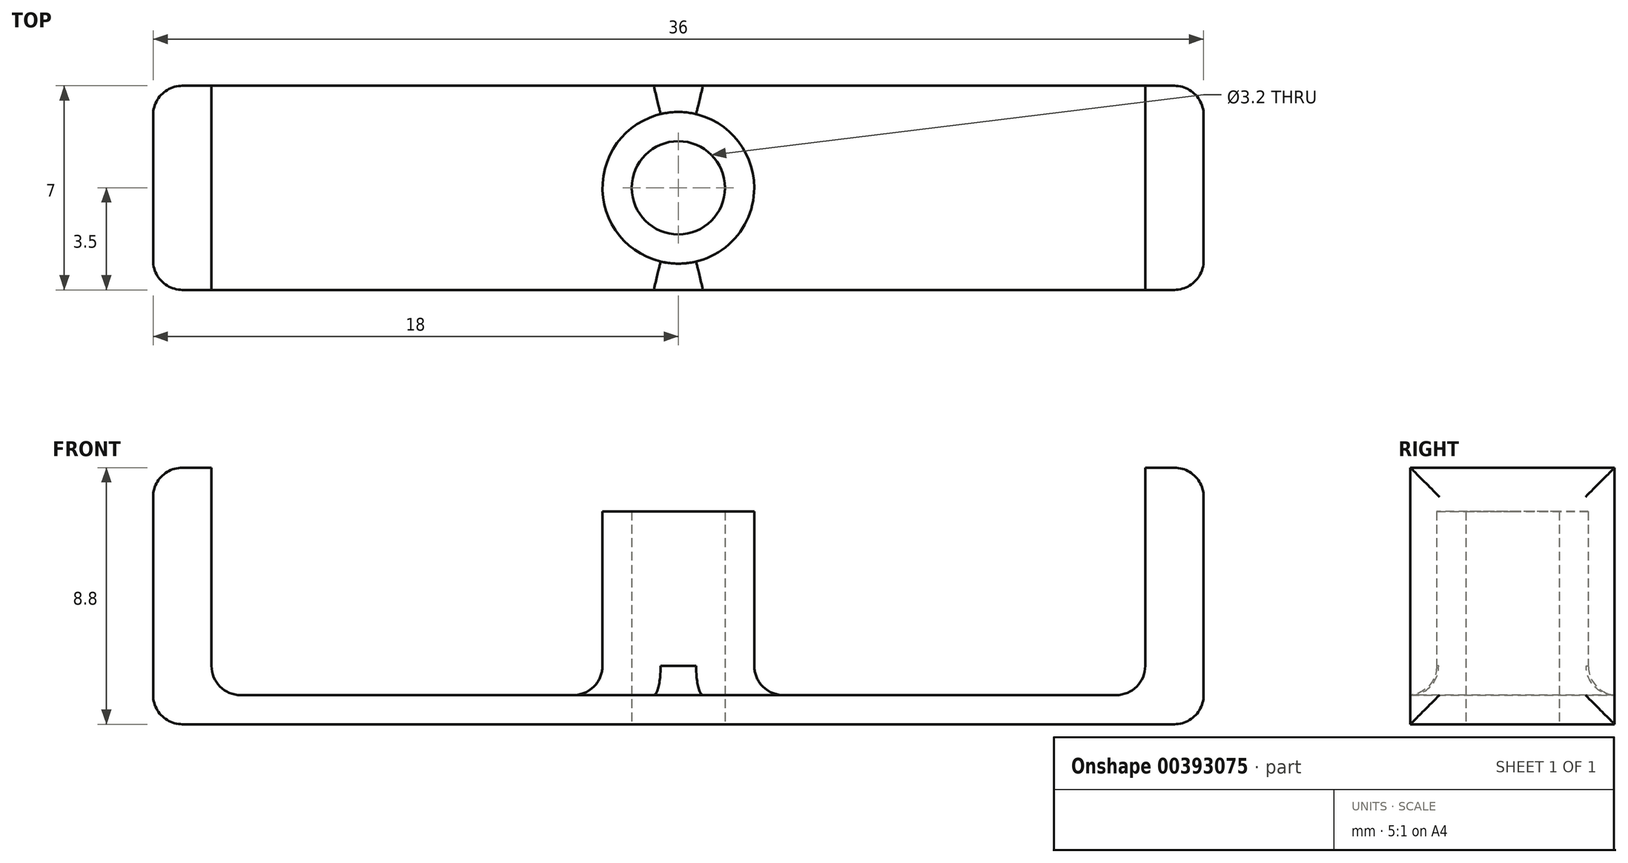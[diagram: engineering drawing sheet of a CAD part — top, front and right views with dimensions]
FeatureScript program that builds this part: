
annotation { "Feature Type Name" : "Feature", "Feature Type Description" : "" }
export const myFeature = defineFeature(function(context is Context, id is Id, definition is map)
    precondition{}
    {
        {
            var Q0;
            Q0=qCreatedBy(makeId("Top.planeOp"),FACE);
            var sketch = newSketch(context, id + "F0", { "sketchPlane" : qUnion([Q0])});
            skLineSegment(sketch, "E0.bottom", {"start": v(18, -3.5) * mm, "end": v(-18, -3.5) * mm});
            skLineSegment(sketch, "E0.top", {"start": v(18, 3.5) * mm, "end": v(-18, 3.5) * mm});
            skLineSegment(sketch, "E0.left", {"start": v(18, -3.5) * mm, "end": v(18, 3.5) * mm});
            skLineSegment(sketch, "E0.right", {"start": v(-18, -3.5) * mm, "end": v(-18, 3.5) * mm});
            skPoint(sketch, "E0.middle", {"position": v(0, 0) * mm});
            skCircle(sketch, "E1", {"center": v(0, 0) * mm, "radius": 1.6 * mm});
            skCircle(sketch, "E2.0", {"center": v(0, 0) * mm, "radius": 2.6 * mm});
            skLineSegment(sketch, "E3", {"start": v(-16, 3.5) * mm, "end": v(-16, -3.5) * mm});
            skLineSegment(sketch, "E4.MirrorCS", {"start": v(16, 3.5) * mm, "end": v(16, -3.5) * mm});
            skSolve(sketch);
        }
        {
            var Q0;
            Q0=makeQuery(id+"F0.imprint","IMPRINT",FACE,{"disambiguationData":[TD([[makeQuery(id+"F0.imprint","IMPRINT",EDGE,{"derivedFrom":sQuery(id+"F0.wireOp",EDGE,"E2.0")}),-1.0]])]});
            var Q1;
            {var subQ0=sQuery(id+"F0.wireOp",EDGE,"E0.right");Q1=makeQuery(id+"F0.imprint","IMPRINT",FACE,{"disambiguationData":[TD([[makeQuery(id+"F0.imprint","IMPRINT",EDGE,{"derivedFrom":subQ0}),-1.0]])]});}
            var Q2;
            {var subQ0=sQuery(id+"F0.wireOp",EDGE,"E0.left");Q2=makeQuery(id+"F0.imprint","IMPRINT",FACE,{"disambiguationData":[TD([[makeQuery(id+"F0.imprint","IMPRINT",EDGE,{"derivedFrom":subQ0}),1.0]])]});}
            var Q3;
            Q3=makeQuery(id+"F0.imprint","IMPRINT",FACE,{"disambiguationData":[TD([[makeQuery(id+"F0.imprint","IMPRINT",EDGE,{"derivedFrom":sQuery(id+"F0.wireOp",EDGE,"E1")}),-1.0]])]});
            extrude(context, id + "F1", {"entities" : qUnion([Q0, Q1, Q2, Q3]), "depth" : 1 * mm});
        }
        {
            var Q0;
            {var subQ0=sQuery(id+"F0.wireOp",EDGE,"E0.right");Q0=makeQuery(id+"F0.imprint","IMPRINT",FACE,{"disambiguationData":[TD([[makeQuery(id+"F0.imprint","IMPRINT",EDGE,{"derivedFrom":subQ0}),-1.0]])]});}
            var Q1;
            {var subQ0=sQuery(id+"F0.wireOp",EDGE,"E0.left");Q1=makeQuery(id+"F0.imprint","IMPRINT",FACE,{"disambiguationData":[TD([[makeQuery(id+"F0.imprint","IMPRINT",EDGE,{"derivedFrom":subQ0}),1.0]])]});}
            extrude(context, id + "F2", {"entities" : qUnion([Q0, Q1]), "operationType" : NewBodyOperationType.ADD, "depth" : 8.8 * mm});
        }
        {
            var Q0;
            Q0=makeQuery(id+"F0.imprint","IMPRINT",FACE,{"disambiguationData":[TD([[makeQuery(id+"F0.imprint","IMPRINT",EDGE,{"derivedFrom":sQuery(id+"F0.wireOp",EDGE,"E1")}),-1.0]])]});
            extrude(context, id + "F3", {"entities" : qUnion([Q0]), "operationType" : NewBodyOperationType.ADD, "depth" : 7.3 * mm});
        }
        {
            var Q0;
            Q0=makeQuery(id+"F2.boolean.opBoolean","INTERSECT",EDGE,{"derivedFrom":[makeQuery(id+"F1.opExtrude","CAP_FACE",FACE,{"disambiguationData":[OSD([sQuery(id+"F0.wireOp",EDGE,"E0.bottom"),sQuery(id+"F0.wireOp",EDGE,"E0.top"),sQuery(id+"F0.wireOp",EDGE,"E0.left"),sQuery(id+"F0.wireOp",EDGE,"E0.right"),sQuery(id+"F0.wireOp",EDGE,"E1")])],"isStart":false}),makeQuery(id+"F2.opExtrude","SWEPT_FACE",FACE,{"disambiguationData":[OSD([sQuery(id+"F0.wireOp",EDGE,"E3")])]})]});
            var Q1;
            Q1=makeQuery(id+"F2.boolean.opBoolean","INTERSECT",EDGE,{"derivedFrom":[makeQuery(id+"F1.opExtrude","CAP_FACE",FACE,{"disambiguationData":[OSD([sQuery(id+"F0.wireOp",EDGE,"E0.bottom"),sQuery(id+"F0.wireOp",EDGE,"E0.top"),sQuery(id+"F0.wireOp",EDGE,"E0.left"),sQuery(id+"F0.wireOp",EDGE,"E0.right"),sQuery(id+"F0.wireOp",EDGE,"E1")])],"isStart":false}),makeQuery(id+"F2.opExtrude","SWEPT_FACE",FACE,{"disambiguationData":[OSD([sQuery(id+"F0.wireOp",EDGE,"E4.MirrorCS")])]})]});
            var Q2;
            Q2=makeQuery(id+"F1.opExtrude","CAP_EDGE",EDGE,{"disambiguationData":[OSD([sQuery(id+"F0.wireOp",EDGE,"E0.right")])],"isStart":true});
            var Q3;
            Q3=makeQuery(id+"F1.opExtrude","CAP_EDGE",EDGE,{"disambiguationData":[OSD([sQuery(id+"F0.wireOp",EDGE,"E0.left")])],"isStart":true});
            var Q4;
            Q4=makeQuery(id+"F2.opExtrude","CAP_EDGE",EDGE,{"disambiguationData":[OSD([sQuery(id+"F0.wireOp",EDGE,"E0.right")])],"isStart":false});
            var Q5;
            Q5=makeQuery(id+"F2.opExtrude","CAP_EDGE",EDGE,{"disambiguationData":[OSD([sQuery(id+"F0.wireOp",EDGE,"E0.left")])],"isStart":false});
            var Q6;
            {var subQ0=sQuery(id+"F0.wireOp",EDGE,"E0.right");var subQ1=sQuery(id+"F0.wireOp",EDGE,"E0.bottom");Q6=makeQuery(id+"F2.boolean.opBoolean","MERGE",EDGE,{"derivedFrom":[makeQuery(id+"F1.opExtrude","SWEPT_EDGE",EDGE,{"disambiguationData":[OSD([subQ1,subQ0])]}),makeQuery(id+"F2.opExtrude","SWEPT_EDGE",EDGE,{"disambiguationData":[OSD([subQ1,subQ0])]})]});}
            var Q7;
            {var subQ0=sQuery(id+"F0.wireOp",EDGE,"E0.right");var subQ1=sQuery(id+"F0.wireOp",EDGE,"E0.top");Q7=makeQuery(id+"F2.boolean.opBoolean","MERGE",EDGE,{"derivedFrom":[makeQuery(id+"F1.opExtrude","SWEPT_EDGE",EDGE,{"disambiguationData":[OSD([subQ1,subQ0])]}),makeQuery(id+"F2.opExtrude","SWEPT_EDGE",EDGE,{"disambiguationData":[OSD([subQ1,subQ0])]})]});}
            var Q8;
            {var subQ0=sQuery(id+"F0.wireOp",EDGE,"E0.left");var subQ1=sQuery(id+"F0.wireOp",EDGE,"E0.bottom");Q8=makeQuery(id+"F2.boolean.opBoolean","MERGE",EDGE,{"derivedFrom":[makeQuery(id+"F1.opExtrude","SWEPT_EDGE",EDGE,{"disambiguationData":[OSD([subQ1,subQ0])]}),makeQuery(id+"F2.opExtrude","SWEPT_EDGE",EDGE,{"disambiguationData":[OSD([subQ1,subQ0])]})]});}
            var Q9;
            {var subQ0=sQuery(id+"F0.wireOp",EDGE,"E0.left");var subQ1=sQuery(id+"F0.wireOp",EDGE,"E0.top");Q9=makeQuery(id+"F2.boolean.opBoolean","MERGE",EDGE,{"derivedFrom":[makeQuery(id+"F1.opExtrude","SWEPT_EDGE",EDGE,{"disambiguationData":[OSD([subQ1,subQ0])]}),makeQuery(id+"F2.opExtrude","SWEPT_EDGE",EDGE,{"disambiguationData":[OSD([subQ1,subQ0])]})]});}
            fillet(context, id + "F4", {"entities" : qUnion([Q0, Q1, Q2, Q3, Q4, Q5, Q6, Q7, Q8, Q9]), "radius" : 1 * mm, "tangentPropagation" : true, "allowEdgeOverflow" : false});
        }
        {
            var Q0;
            Q0=makeQuery(id+"F3.boolean.opBoolean","INTERSECT",EDGE,{"derivedFrom":[makeQuery(id+"F1.opExtrude","CAP_FACE",FACE,{"disambiguationData":[OSD([sQuery(id+"F0.wireOp",EDGE,"E0.bottom"),sQuery(id+"F0.wireOp",EDGE,"E0.top"),sQuery(id+"F0.wireOp",EDGE,"E0.left"),sQuery(id+"F0.wireOp",EDGE,"E0.right"),sQuery(id+"F0.wireOp",EDGE,"E1")])],"isStart":false}),makeQuery(id+"F3.opExtrude","SWEPT_FACE",FACE,{"disambiguationData":[OSD([sQuery(id+"F0.wireOp",EDGE,"E2.0")])]})]});
            fillet(context, id + "F5", {"entities" : qUnion([Q0]), "radius" : 1 * mm, "tangentPropagation" : true, "allowEdgeOverflow" : false});
        }
    });
